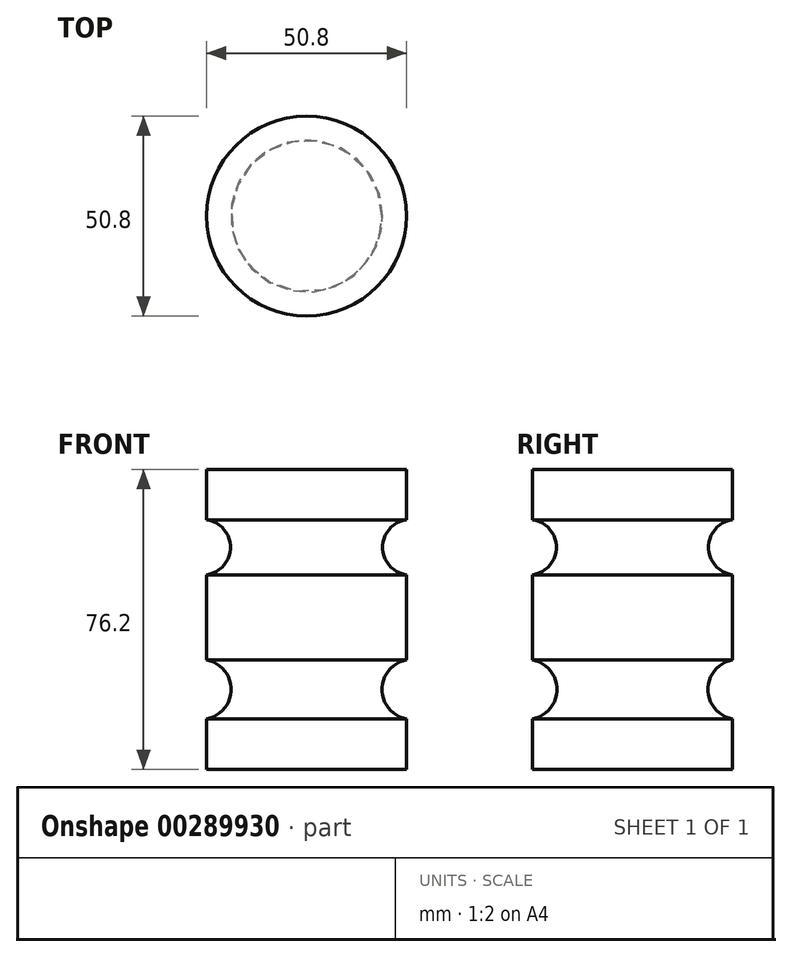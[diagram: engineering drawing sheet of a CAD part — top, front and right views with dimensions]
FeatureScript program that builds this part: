
annotation { "Feature Type Name" : "Feature", "Feature Type Description" : "" }
export const myFeature = defineFeature(function(context is Context, id is Id, definition is map)
    precondition{}
    {
        {
            var Q0;
            Q0=qCreatedBy(makeId("Front.planeOp"),FACE);
            var sketch = newSketch(context, id + "F0", { "sketchPlane" : qUnion([Q0])});
            skLineSegment(sketch, "E0.bottom", {"start": v(-25.4, 76.2) * mm, "end": v(0, 76.2) * mm});
            skLineSegment(sketch, "E0.top", {"start": v(-25.4, 0) * mm, "end": v(0, 0) * mm});
            skLineSegment(sketch, "E0.left", {"start": v(-25.4, 76.2) * mm, "end": v(-25.4, 0) * mm});
            skLineSegment(sketch, "E0.right", {"start": v(0, 76.2) * mm, "end": v(0, 63.43) * mm});
            skArc(sketch, "E1", {"start": v(0, 63.43) * mm, "mid": v(-6.08, 56.43) * mm, "end": v(0, 49.43) * mm});
            skArc(sketch, "E2", {"start": v(0, 27.81) * mm, "mid": v(-6.24, 20.32) * mm, "end": v(0, 12.83) * mm});
            skLineSegment(sketch, "E3.trimOffspring", {"start": v(0, 49.43) * mm, "end": v(0, 27.81) * mm});
            skLineSegment(sketch, "E4.trimOffspring", {"start": v(0, 12.83) * mm, "end": v(0, 0) * mm});
            skSolve(sketch);
        }
        {
            var Q0;
            Q0 = qSketchRegion(id + "F0", true);
            var Q1;
            Q1=sQuery(id+"F0.wireOp",EDGE,"E0.left");
            revolve(context, id + "F1", {"entities" : qUnion([Q0]), "axis" : qUnion([Q1]), "revolveType" : RevolveType.FULL});
        }
    });
